# Revit family: bimlib_narujnyeblokisistemakondicionirovaniya_mrv-5_18-26hp_haier
name_source: partatom
category: Оборудование
units: mm (PartAtom-declared; Revit-internal decimal feet)

## family parameters
Всегда вертикально = Да
На основе рабочей плоскости = Нет
Общий = Нет
При загрузке вырезать с полостями = Нет
Размер круглого соединителя = Использовать диаметр
Тип детали = Нормальный
Точка расчета площади = Нет

## types (5) — shared parameters
ADSK_URL документации изделия = https://haierproff.ru
ADSK_URL страницы изделия = https://haierproff.ru
ADSK_Версия Revit = 2017
ADSK_Группирование = VRF-системы MRV 5
ADSK_Единица измерения = шт.
ADSK_Завод-изготовитель = Haier Group
ADSK_Классификация нагрузок = ОВК
ADSK_Количество = 1
ADSK_Количество фаз = 3
ADSK_Коэффициент мощности = 1
ADSK_Напряжение = 400 В
ADSK_Обозначение = MRV 5
ADSK_Размер_Высота = 1690 мм
ADSK_Размер_Глубина = 750 мм
ADSK_Размер_Ширина = 1410 мм
BL_BIM library = https://bimlib.pro
HG_URL поставщика = www.haierproff.ru
URL = www.haier.com
Диаметр_Газ = 28.58 мм
Диаметр_Жидкость = 15.88 мм
Заправка хладагента = 10.00 кг
Изготовитель = Haier Group
Производитель компрессора = MITSUBISHI ELECTRIC
Работа на обогрев = Нет
Рабочий диапазон_Обогрев = -23 ~ 21
Рабочий диапазон_Охлаждение = -5 ~ 50
Тип компрессора = DC INV. СПИРАЛ.
Тип хладагента = R410A
Частота тока = 50 Гц
zero-valued in all types: Отметка по умолчанию

## per-type parameters (varying)
| type | ADSK_Код изделия | ADSK_Масса | ADSK_Наименование | ADSK_Наименование краткое | ADSK_Номинальная мощность | ADSK_Полная мощность | ADSK_Расход воздуха | Звуковая мощность | Звуковое давление | Обогрев_Максимальная потребляемая мощность | Обогрев_Максимальный ток | Обогрев_Номинальная потребляемая мощность | Обогрев_Номинальный ток | Охлаждение_Максимальная потребляемая мощность | Охлаждение_Максимальный ток | Охлаждение_Номинальная потребляемая мощность | Охлаждение_Номинальный ток | Теплопроизводительность | Холодопроизводительность |
| AV18IMVEVA_18HP_HAIER | AV18IMVEVA | 287 | Наружный блок VRF-системы кондиционирования MRV-5, 18HP | VRF-системы MRV 5, 18HP | 14300 Вт | 14300 В·А | 17000.0 м³/ч | 72 | 61 | 18 кВт | 30 А | 13 кВт | 23 А | 21 кВт | 36 А | 14 кВт | 24 А | 57 кВт | 50 кВт |
| AV20IMVEVA_20HP_HAIER | AV20IMVEVA | 370 | Наружный блок VRF-системы кондиционирования MRV-5, 20HP | VRF-системы MRV 5, 20HP | 15100 Вт | 15100 В·А | 17000.0 м³/ч | 72 | 61 | 23 кВт | 38 А | 15 кВт | 25 А | 25 кВт | 42 А | 15 кВт | 25 А | 62 кВт | 56 кВт |
| AV22IMVEVA_22HP_HAIER | AV22IMVEVA | 370 | Наружный блок VRF-системы кондиционирования MRV-5, 22HP | VRF-системы MRV 5, 22HP | 16500 Вт | 16500 В·А | 18000.0 м³/ч | 72 | 61 | 26 кВт | 43 А | 15 кВт | 26 А | 29 кВт | 48 А | 17 кВт | 28 А | 69 кВт | 62 кВт |
| AV24IMVEVA_24HP_HAIER | AV24IMVEVA | 370 | Наружный блок VRF-системы кондиционирования MRV-5, 24HP | VRF-системы MRV 5, 24HP | 17600 Вт | 17600 В·А | 18000.0 м³/ч | 73 | 62 | 27 кВт | 45 А | 17 кВт | 28 А | 29 кВт | 49 А | 18 кВт | 30 А | 73 кВт | 68 кВт |
| AV26IMVEVA_26HP_HAIER | AV26IMVEVA | 370 | Наружный блок VRF-системы кондиционирования MRV-5, 26HP | VRF-системы MRV 5, 26HP | 18800 Вт | 18800 В·А | 19000.0 м³/ч | 73 | 62 | 30 кВт | 51 А | 18 кВт | 30 А | 33 кВт | 56 А | 19 кВт | 32 А | 83 кВт | 74 кВт |
